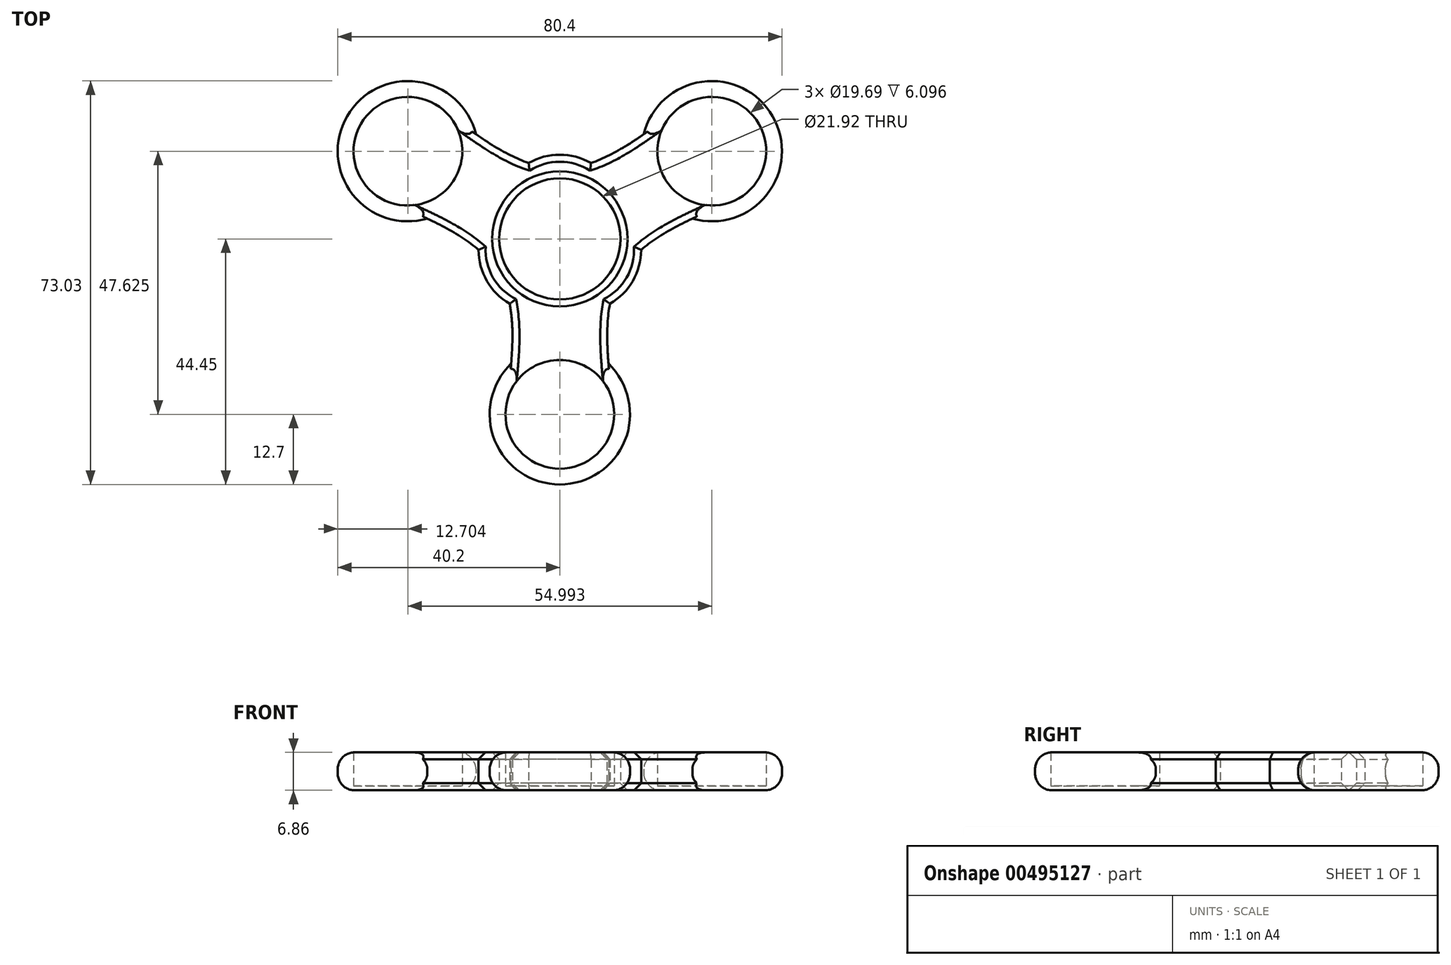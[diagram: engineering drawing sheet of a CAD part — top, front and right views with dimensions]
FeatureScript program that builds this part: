
annotation { "Feature Type Name" : "Feature", "Feature Type Description" : "" }
export const myFeature = defineFeature(function(context is Context, id is Id, definition is map)
    precondition{}
    {
        {
            var Q0;
            Q0=qCreatedBy(makeId("Top.planeOp"),FACE);
            var sketch = newSketch(context, id + "F0", { "sketchPlane" : qUnion([Q0])});
            skCircle(sketch, "E0", {"center": v(0, 0) * mm, "radius": 10.96 * mm});
            skCircle(sketch, "E1", {"center": v(0, 0) * mm, "radius": 12.7 * mm});
            skLineSegment(sketch, "E2", {"start": v(0, 0) * mm, "end": v(0, -12.7) * mm});
            skCircle(sketch, "E3.cCircle", {"center": v(0, 0) * mm, "radius": 12.7 * mm, "construction": true});
            skLineSegment(sketch, "E3.0", {"start": v(0, -12.7) * mm, "end": v(-11, 6.35) * mm});
            skLineSegment(sketch, "E3.1", {"start": v(-11, 6.35) * mm, "end": v(11, 6.35) * mm});
            skLineSegment(sketch, "E3.2", {"start": v(11, 6.35) * mm, "end": v(0, -12.7) * mm});
            skLineSegment(sketch, "E4", {"start": v(-11, 6.35) * mm, "end": v(0, 0) * mm});
            skLineSegment(sketch, "E5", {"start": v(0, 0) * mm, "end": v(11, 6.35) * mm});
            skLineSegment(sketch, "E6", {"start": v(-11, 6.35) * mm, "end": v(-27.5, 15.88) * mm});
            skLineSegment(sketch, "E7", {"start": v(11, 6.35) * mm, "end": v(27.5, 15.88) * mm});
            skLineSegment(sketch, "E8", {"start": v(0, -12.7) * mm, "end": v(0, -31.75) * mm});
            skCircle(sketch, "E9", {"center": v(-27.5, 15.87) * mm, "radius": 9.84 * mm});
            skCircle(sketch, "E10", {"center": v(27.5, 15.87) * mm, "radius": 9.84 * mm});
            skCircle(sketch, "E11", {"center": v(0, -31.75) * mm, "radius": 9.84 * mm});
            skLineSegment(sketch, "E12", {"start": v(-27.5, 15.87) * mm, "end": v(-32.42, 7.35) * mm});
            skLineSegment(sketch, "E13", {"start": v(-27.5, 15.87) * mm, "end": v(-22.58, 24.4) * mm});
            skLineSegment(sketch, "E14", {"start": v(27.5, 15.87) * mm, "end": v(22.58, 24.4) * mm});
            skLineSegment(sketch, "E15", {"start": v(27.5, 15.88) * mm, "end": v(32.42, 7.35) * mm});
            skLineSegment(sketch, "E16", {"start": v(0, -31.75) * mm, "end": v(-9.84, -31.75) * mm});
            skLineSegment(sketch, "E17", {"start": v(0, -31.75) * mm, "end": v(9.84, -31.75) * mm});
            skCircle(sketch, "E18", {"center": v(-27.5, 15.87) * mm, "radius": 12.7 * mm});
            skCircle(sketch, "E19", {"center": v(27.5, 15.87) * mm, "radius": 12.7 * mm});
            skCircle(sketch, "E20", {"center": v(0, -31.75) * mm, "radius": 12.7 * mm});
            skPoint(sketch, "E21", {"position": v(-5.5, -3.17) * mm});
            skPoint(sketch, "E22", {"position": v(0, 6.35) * mm});
            skPoint(sketch, "E23", {"position": v(5.5, -3.18) * mm});
            skLineSegment(sketch, "E24", {"start": v(-11, -6.35) * mm, "end": v(-13.18, -7.64) * mm});
            skLineSegment(sketch, "E25", {"start": v(11, -6.35) * mm, "end": v(13.2, -7.62) * mm});
            skArc(sketch, "E26", {"start": v(-11, 6.35) * mm, "mid": v(-13.2, -7.62) * mm, "end": v(0, -12.7) * mm});
            skArc(sketch, "E27", {"start": v(0, -12.7) * mm, "mid": v(13.2, -7.62) * mm, "end": v(11, 6.35) * mm});
            skLineSegment(sketch, "E28", {"start": v(0, 12.7) * mm, "end": v(0, 15.24) * mm});
            skArc(sketch, "E29", {"start": v(11, 6.35) * mm, "mid": v(0, 15.24) * mm, "end": v(-11, 6.35) * mm});
            skFitSpline(sketch, "E30", {"points": [v(-32.42, 7.35) * mm, v(-11, -6.35) * mm, v(-9.84, -31.75) * mm], "startDerivative": vector(52.41, -22.24) * mm, "endDerivative": vector(-6.95, -56.51) * mm});
            skFitSpline(sketch, "E31", {"points": [v(9.84, -31.75) * mm, v(11, -6.35) * mm, v(32.42, 7.35) * mm], "startDerivative": vector(-6.95, 56.51) * mm, "endDerivative": vector(52.41, 22.24) * mm});
            skFitSpline(sketch, "E32", {"points": [v(22.58, 24.4) * mm, v(0, 12.7) * mm, v(-22.58, 24.4) * mm], "startDerivative": vector(-45.47, -34.27) * mm, "endDerivative": vector(-45.47, 34.27) * mm});
            skSolve(sketch);
        }
        {
            var Q0;
            Q0 = qSketchRegion(id + "F0", true);
            var Q1;
            {var subQ1=sQuery(id+"F0.wireOp",EDGE,"E3.0");var subQ4=sQuery(id+"F0.wireOp",EDGE,"E0");var subQ8=makeQuery(id+"F0.imprint","INTERSECT",VERTEX,{"disambiguationData":[OD(0.0)],"derivedFrom":[subQ4,subQ1]});Q1=makeQuery(id+"F0.imprint","IMPRINT",FACE,{"disambiguationData":[TD([[makeQuery(id+"F0.imprint","IMPRINT",EDGE,{"disambiguationData":[TD([[subQ8,-1.0]])],"derivedFrom":subQ4}),-1.0]])]});}
            var Q2;
            {var subQ1=sQuery(id+"F0.wireOp",EDGE,"E3.1");var subQ4=sQuery(id+"F0.wireOp",EDGE,"E0");var subQ8=makeQuery(id+"F0.imprint","INTERSECT",VERTEX,{"disambiguationData":[OD(0.0)],"derivedFrom":[subQ4,subQ1]});Q2=makeQuery(id+"F0.imprint","IMPRINT",FACE,{"disambiguationData":[TD([[makeQuery(id+"F0.imprint","IMPRINT",EDGE,{"disambiguationData":[TD([[subQ8,-1.0]])],"derivedFrom":subQ4}),-1.0]])]});}
            var Q3;
            {var subQ1=sQuery(id+"F0.wireOp",EDGE,"E3.2");var subQ6=sQuery(id+"F0.wireOp",EDGE,"E0");var subQ8=makeQuery(id+"F0.imprint","INTERSECT",VERTEX,{"disambiguationData":[OD(0.0)],"derivedFrom":[subQ6,subQ1]});Q3=makeQuery(id+"F0.imprint","IMPRINT",FACE,{"disambiguationData":[TD([[makeQuery(id+"F0.imprint","IMPRINT",EDGE,{"disambiguationData":[TD([[subQ8,1.0]])],"derivedFrom":subQ6}),-1.0]])]});}
            var Q4;
            {var subQ0=sQuery(id+"F0.wireOp",EDGE,"E2");var subQ1=sQuery(id+"F0.wireOp",EDGE,"E0");var subQ2=makeQuery(id+"F0.imprint","INTERSECT",VERTEX,{"derivedFrom":[subQ1,subQ0]});Q4=makeQuery(id+"F0.imprint","IMPRINT",FACE,{"disambiguationData":[TD([[makeQuery(id+"F0.imprint","IMPRINT",EDGE,{"disambiguationData":[TD([[subQ2,-1.0]])],"derivedFrom":subQ1}),-1.0]])]});}
            var Q5;
            {var subQ0=sQuery(id+"F0.wireOp",EDGE,"E3.0");var subQ1=sQuery(id+"F0.wireOp",EDGE,"E0");var subQ2=makeQuery(id+"F0.imprint","INTERSECT",VERTEX,{"disambiguationData":[OD(1.0)],"derivedFrom":[subQ1,subQ0]});Q5=makeQuery(id+"F0.imprint","IMPRINT",FACE,{"disambiguationData":[TD([[makeQuery(id+"F0.imprint","IMPRINT",EDGE,{"disambiguationData":[TD([[subQ2,-1.0]])],"derivedFrom":subQ1}),-1.0]])]});}
            var Q6;
            {var subQ0=sQuery(id+"F0.wireOp",EDGE,"E5");var subQ1=sQuery(id+"F0.wireOp",EDGE,"E0");var subQ2=makeQuery(id+"F0.imprint","INTERSECT",VERTEX,{"derivedFrom":[subQ1,subQ0]});Q6=makeQuery(id+"F0.imprint","IMPRINT",FACE,{"disambiguationData":[TD([[makeQuery(id+"F0.imprint","IMPRINT",EDGE,{"disambiguationData":[TD([[subQ2,1.0]])],"derivedFrom":subQ1}),-1.0]])]});}
            var Q7;
            {var subQ0=sQuery(id+"F0.wireOp",EDGE,"E5");var subQ1=sQuery(id+"F0.wireOp",EDGE,"E0");var subQ2=makeQuery(id+"F0.imprint","INTERSECT",VERTEX,{"derivedFrom":[subQ1,subQ0]});Q7=makeQuery(id+"F0.imprint","IMPRINT",FACE,{"disambiguationData":[TD([[makeQuery(id+"F0.imprint","IMPRINT",EDGE,{"disambiguationData":[TD([[subQ2,-1.0]])],"derivedFrom":subQ1}),-1.0]])]});}
            var Q8;
            {var subQ0=sQuery(id+"F0.wireOp",EDGE,"E4");var subQ1=sQuery(id+"F0.wireOp",EDGE,"E0");var subQ2=makeQuery(id+"F0.imprint","INTERSECT",VERTEX,{"derivedFrom":[subQ1,subQ0]});Q8=makeQuery(id+"F0.imprint","IMPRINT",FACE,{"disambiguationData":[TD([[makeQuery(id+"F0.imprint","IMPRINT",EDGE,{"disambiguationData":[TD([[subQ2,-1.0]])],"derivedFrom":subQ1}),-1.0]])]});}
            var Q9;
            {var subQ0=sQuery(id+"F0.wireOp",EDGE,"E3.1");var subQ1=sQuery(id+"F0.wireOp",EDGE,"E0");var subQ2=makeQuery(id+"F0.imprint","INTERSECT",VERTEX,{"disambiguationData":[OD(1.0)],"derivedFrom":[subQ1,subQ0]});Q9=makeQuery(id+"F0.imprint","IMPRINT",FACE,{"disambiguationData":[TD([[makeQuery(id+"F0.imprint","IMPRINT",EDGE,{"disambiguationData":[TD([[subQ2,-1.0]])],"derivedFrom":subQ1}),-1.0]])]});}
            extrude(context, id + "F1", {"entities" : qUnion([Q0, Q1, Q2, Q3, Q4, Q5, Q6, Q7, Q8, Q9]), "depth" : 6.86 * mm, "offsetDistance" : 25.4 * mm});
        }
        {
            var Q0;
            Q0=makeQuery(id+"F1.opExtrude","CAP_EDGE",EDGE,{"disambiguationData":[OSD([sQuery(id+"F0.wireOp",EDGE,"E0")])],"isStart":true});
            var Q1;
            Q1=makeQuery(id+"F1.opExtrude","CAP_EDGE",EDGE,{"disambiguationData":[OSD([sQuery(id+"F0.wireOp",EDGE,"E0")])],"isStart":false});
            chamfer(context, id + "F2", {"entities" : qUnion([Q0, Q1]), "width" : 1.27 * mm, "tangentPropagation" : true});
        }
        {
            var Q0;
            {var subQ0=sQuery(id+"F0.wireOp",EDGE,"E31");Q0=makeQuery(id+"F1.opExtrude","CAP_EDGE",EDGE,{"disambiguationData":[OSD([subQ0]),TDD([makeQuery(id+"F0.imprint","IMPRINT",EDGE,{"disambiguationData":[TD([[makeQuery(id+"F0.imprint","INTERSECT",VERTEX,{"derivedFrom":[sQuery(id+"F0.wireOp",EDGE,"E20"),subQ0]}),-1.0]])],"derivedFrom":subQ0})])],"isStart":false});}
            var Q1;
            Q1=makeQuery(id+"F1.opExtrude","CAP_EDGE",EDGE,{"disambiguationData":[OSD([sQuery(id+"F0.wireOp",EDGE,"E27")])],"isStart":false});
            var Q2;
            {var subQ0=sQuery(id+"F0.wireOp",EDGE,"E31");Q2=makeQuery(id+"F1.opExtrude","CAP_EDGE",EDGE,{"disambiguationData":[OSD([subQ0]),TDD([makeQuery(id+"F0.imprint","IMPRINT",EDGE,{"disambiguationData":[TD([[makeQuery(id+"F0.imprint","INTERSECT",VERTEX,{"derivedFrom":[sQuery(id+"F0.wireOp",EDGE,"E19"),subQ0]}),1.0]])],"derivedFrom":subQ0})])],"isStart":false});}
            var Q3;
            {var subQ0=sQuery(id+"F0.wireOp",EDGE,"E32");Q3=makeQuery(id+"F1.opExtrude","CAP_EDGE",EDGE,{"disambiguationData":[OSD([subQ0]),TDD([makeQuery(id+"F0.imprint","IMPRINT",EDGE,{"disambiguationData":[TD([[makeQuery(id+"F0.imprint","INTERSECT",VERTEX,{"derivedFrom":[sQuery(id+"F0.wireOp",EDGE,"E19"),subQ0]}),-1.0]])],"derivedFrom":subQ0})])],"isStart":false});}
            var Q4;
            Q4=makeQuery(id+"F1.opExtrude","CAP_EDGE",EDGE,{"disambiguationData":[OSD([sQuery(id+"F0.wireOp",EDGE,"E29")])],"isStart":false});
            var Q5;
            {var subQ0=sQuery(id+"F0.wireOp",EDGE,"E32");Q5=makeQuery(id+"F1.opExtrude","CAP_EDGE",EDGE,{"disambiguationData":[OSD([subQ0]),TDD([makeQuery(id+"F0.imprint","IMPRINT",EDGE,{"disambiguationData":[TD([[makeQuery(id+"F0.imprint","INTERSECT",VERTEX,{"derivedFrom":[sQuery(id+"F0.wireOp",EDGE,"E18"),subQ0]}),1.0]])],"derivedFrom":subQ0})])],"isStart":false});}
            var Q6;
            {var subQ0=sQuery(id+"F0.wireOp",EDGE,"E30");Q6=makeQuery(id+"F1.opExtrude","CAP_EDGE",EDGE,{"disambiguationData":[OSD([subQ0]),TDD([makeQuery(id+"F0.imprint","IMPRINT",EDGE,{"disambiguationData":[TD([[makeQuery(id+"F0.imprint","INTERSECT",VERTEX,{"derivedFrom":[sQuery(id+"F0.wireOp",EDGE,"E18"),subQ0]}),-1.0]])],"derivedFrom":subQ0})])],"isStart":false});}
            var Q7;
            {var subQ0=sQuery(id+"F0.wireOp",EDGE,"E30");Q7=makeQuery(id+"F1.opExtrude","CAP_EDGE",EDGE,{"disambiguationData":[OSD([subQ0]),TDD([makeQuery(id+"F0.imprint","IMPRINT",EDGE,{"disambiguationData":[TD([[makeQuery(id+"F0.imprint","INTERSECT",VERTEX,{"derivedFrom":[sQuery(id+"F0.wireOp",EDGE,"E18"),subQ0]}),-1.0]])],"derivedFrom":subQ0})])],"isStart":true});}
            var Q8;
            Q8=makeQuery(id+"F1.opExtrude","CAP_EDGE",EDGE,{"disambiguationData":[OSD([sQuery(id+"F0.wireOp",EDGE,"E26")])],"isStart":true});
            var Q9;
            Q9=makeQuery(id+"F1.opExtrude","CAP_EDGE",EDGE,{"disambiguationData":[OSD([sQuery(id+"F0.wireOp",EDGE,"E26")])],"isStart":false});
            var Q10;
            {var subQ0=sQuery(id+"F0.wireOp",EDGE,"E30");Q10=makeQuery(id+"F1.opExtrude","CAP_EDGE",EDGE,{"disambiguationData":[OSD([subQ0]),TDD([makeQuery(id+"F0.imprint","IMPRINT",EDGE,{"disambiguationData":[TD([[makeQuery(id+"F0.imprint","INTERSECT",VERTEX,{"derivedFrom":[sQuery(id+"F0.wireOp",EDGE,"E20"),subQ0]}),1.0]])],"derivedFrom":subQ0})])],"isStart":true});}
            var Q11;
            {var subQ0=sQuery(id+"F0.wireOp",EDGE,"E30");Q11=makeQuery(id+"F1.opExtrude","CAP_EDGE",EDGE,{"disambiguationData":[OSD([subQ0]),TDD([makeQuery(id+"F0.imprint","IMPRINT",EDGE,{"disambiguationData":[TD([[makeQuery(id+"F0.imprint","INTERSECT",VERTEX,{"derivedFrom":[sQuery(id+"F0.wireOp",EDGE,"E20"),subQ0]}),1.0]])],"derivedFrom":subQ0})])],"isStart":false});}
            var Q12;
            {var subQ0=sQuery(id+"F0.wireOp",EDGE,"E31");Q12=makeQuery(id+"F1.opExtrude","CAP_EDGE",EDGE,{"disambiguationData":[OSD([subQ0]),TDD([makeQuery(id+"F0.imprint","IMPRINT",EDGE,{"disambiguationData":[TD([[makeQuery(id+"F0.imprint","INTERSECT",VERTEX,{"derivedFrom":[sQuery(id+"F0.wireOp",EDGE,"E20"),subQ0]}),-1.0]])],"derivedFrom":subQ0})])],"isStart":true});}
            var Q13;
            Q13=makeQuery(id+"F1.opExtrude","CAP_EDGE",EDGE,{"disambiguationData":[OSD([sQuery(id+"F0.wireOp",EDGE,"E27")])],"isStart":true});
            var Q14;
            {var subQ0=sQuery(id+"F0.wireOp",EDGE,"E31");Q14=makeQuery(id+"F1.opExtrude","CAP_EDGE",EDGE,{"disambiguationData":[OSD([subQ0]),TDD([makeQuery(id+"F0.imprint","IMPRINT",EDGE,{"disambiguationData":[TD([[makeQuery(id+"F0.imprint","INTERSECT",VERTEX,{"derivedFrom":[sQuery(id+"F0.wireOp",EDGE,"E19"),subQ0]}),1.0]])],"derivedFrom":subQ0})])],"isStart":true});}
            var Q15;
            {var subQ0=sQuery(id+"F0.wireOp",EDGE,"E32");Q15=makeQuery(id+"F1.opExtrude","CAP_EDGE",EDGE,{"disambiguationData":[OSD([subQ0]),TDD([makeQuery(id+"F0.imprint","IMPRINT",EDGE,{"disambiguationData":[TD([[makeQuery(id+"F0.imprint","INTERSECT",VERTEX,{"derivedFrom":[sQuery(id+"F0.wireOp",EDGE,"E19"),subQ0]}),-1.0]])],"derivedFrom":subQ0})])],"isStart":true});}
            var Q16;
            Q16=makeQuery(id+"F1.opExtrude","CAP_EDGE",EDGE,{"disambiguationData":[OSD([sQuery(id+"F0.wireOp",EDGE,"E29")])],"isStart":true});
            var Q17;
            {var subQ0=sQuery(id+"F0.wireOp",EDGE,"E32");Q17=makeQuery(id+"F1.opExtrude","CAP_EDGE",EDGE,{"disambiguationData":[OSD([subQ0]),TDD([makeQuery(id+"F0.imprint","IMPRINT",EDGE,{"disambiguationData":[TD([[makeQuery(id+"F0.imprint","INTERSECT",VERTEX,{"derivedFrom":[sQuery(id+"F0.wireOp",EDGE,"E18"),subQ0]}),1.0]])],"derivedFrom":subQ0})])],"isStart":true});}
            chamfer(context, id + "F3", {"entities" : qUnion([Q0, Q1, Q2, Q3, Q4, Q5, Q6, Q7, Q8, Q9, Q10, Q11, Q12, Q13, Q14, Q15, Q16, Q17]), "width" : 1.27 * mm, "tangentPropagation" : true});
        }
        {
            var Q0;
            {var subQ0=sQuery(id+"F0.wireOp",EDGE,"E12");Q0=makeQuery(id+"F0.imprint","IMPRINT",FACE,{"disambiguationData":[TD([[makeQuery(id+"F0.imprint","IMPRINT",EDGE,{"derivedFrom":subQ0}),-1.0]])]});}
            var Q1;
            {var subQ0=sQuery(id+"F0.wireOp",EDGE,"E12");Q1=makeQuery(id+"F0.imprint","IMPRINT",FACE,{"disambiguationData":[TD([[makeQuery(id+"F0.imprint","IMPRINT",EDGE,{"derivedFrom":subQ0}),1.0]])]});}
            var Q2;
            {var subQ0=sQuery(id+"F0.wireOp",EDGE,"E13");Q2=makeQuery(id+"F0.imprint","IMPRINT",FACE,{"disambiguationData":[TD([[makeQuery(id+"F0.imprint","IMPRINT",EDGE,{"derivedFrom":subQ0}),-1.0]])]});}
            var Q3;
            {var subQ0=sQuery(id+"F0.wireOp",EDGE,"E14");Q3=makeQuery(id+"F0.imprint","IMPRINT",FACE,{"disambiguationData":[TD([[makeQuery(id+"F0.imprint","IMPRINT",EDGE,{"derivedFrom":subQ0}),1.0]])]});}
            var Q4;
            {var subQ0=sQuery(id+"F0.wireOp",EDGE,"E14");Q4=makeQuery(id+"F0.imprint","IMPRINT",FACE,{"disambiguationData":[TD([[makeQuery(id+"F0.imprint","IMPRINT",EDGE,{"derivedFrom":subQ0}),-1.0]])]});}
            var Q5;
            {var subQ0=sQuery(id+"F0.wireOp",EDGE,"E15");Q5=makeQuery(id+"F0.imprint","IMPRINT",FACE,{"disambiguationData":[TD([[makeQuery(id+"F0.imprint","IMPRINT",EDGE,{"derivedFrom":subQ0}),-1.0]])]});}
            var Q6;
            {var subQ0=sQuery(id+"F0.wireOp",EDGE,"E16");Q6=makeQuery(id+"F0.imprint","IMPRINT",FACE,{"disambiguationData":[TD([[makeQuery(id+"F0.imprint","IMPRINT",EDGE,{"derivedFrom":subQ0}),-1.0]])]});}
            var Q7;
            {var subQ0=sQuery(id+"F0.wireOp",EDGE,"E17");Q7=makeQuery(id+"F0.imprint","IMPRINT",FACE,{"disambiguationData":[TD([[makeQuery(id+"F0.imprint","IMPRINT",EDGE,{"derivedFrom":subQ0}),1.0]])]});}
            var Q8;
            {var subQ0=sQuery(id+"F0.wireOp",EDGE,"E16");Q8=makeQuery(id+"F0.imprint","IMPRINT",FACE,{"disambiguationData":[TD([[makeQuery(id+"F0.imprint","IMPRINT",EDGE,{"derivedFrom":subQ0}),1.0]])]});}
            var Q9;
            {var subQ0=sQuery(id+"F0.wireOp",EDGE,"E32");var subQ1=sQuery(id+"F0.wireOp",EDGE,"E10");var subQ3=makeQuery(id+"F0.imprint","INTERSECT",VERTEX,{"derivedFrom":[subQ1,subQ0]});Q9=makeQuery(id+"F0.imprint","IMPRINT",FACE,{"disambiguationData":[TD([[makeQuery(id+"F0.imprint","IMPRINT",EDGE,{"disambiguationData":[TD([[subQ3,1.0]])],"derivedFrom":subQ1}),1.0]])]});}
            var Q10;
            {var subQ0=sQuery(id+"F0.wireOp",EDGE,"E31");var subQ1=sQuery(id+"F0.wireOp",EDGE,"E10");var subQ3=makeQuery(id+"F0.imprint","INTERSECT",VERTEX,{"derivedFrom":[subQ1,subQ0]});Q10=makeQuery(id+"F0.imprint","IMPRINT",FACE,{"disambiguationData":[TD([[makeQuery(id+"F0.imprint","IMPRINT",EDGE,{"disambiguationData":[TD([[subQ3,-1.0]])],"derivedFrom":subQ1}),1.0]])]});}
            var Q11;
            {var subQ0=sQuery(id+"F0.wireOp",EDGE,"E32");var subQ1=sQuery(id+"F0.wireOp",EDGE,"E9");var subQ3=makeQuery(id+"F0.imprint","INTERSECT",VERTEX,{"derivedFrom":[subQ1,subQ0]});Q11=makeQuery(id+"F0.imprint","IMPRINT",FACE,{"disambiguationData":[TD([[makeQuery(id+"F0.imprint","IMPRINT",EDGE,{"disambiguationData":[TD([[subQ3,-1.0]])],"derivedFrom":subQ1}),1.0]])]});}
            var Q12;
            {var subQ0=sQuery(id+"F0.wireOp",EDGE,"E30");var subQ1=sQuery(id+"F0.wireOp",EDGE,"E9");var subQ3=makeQuery(id+"F0.imprint","INTERSECT",VERTEX,{"derivedFrom":[subQ1,subQ0]});Q12=makeQuery(id+"F0.imprint","IMPRINT",FACE,{"disambiguationData":[TD([[makeQuery(id+"F0.imprint","IMPRINT",EDGE,{"disambiguationData":[TD([[subQ3,1.0]])],"derivedFrom":subQ1}),1.0]])]});}
            var Q13;
            {var subQ0=sQuery(id+"F0.wireOp",EDGE,"E30");var subQ1=sQuery(id+"F0.wireOp",EDGE,"E11");var subQ3=makeQuery(id+"F0.imprint","INTERSECT",VERTEX,{"derivedFrom":[subQ1,subQ0]});Q13=makeQuery(id+"F0.imprint","IMPRINT",FACE,{"disambiguationData":[TD([[makeQuery(id+"F0.imprint","IMPRINT",EDGE,{"disambiguationData":[TD([[subQ3,-1.0]])],"derivedFrom":subQ1}),1.0]])]});}
            var Q14;
            {var subQ0=sQuery(id+"F0.wireOp",EDGE,"E31");var subQ1=sQuery(id+"F0.wireOp",EDGE,"E11");var subQ3=makeQuery(id+"F0.imprint","INTERSECT",VERTEX,{"derivedFrom":[subQ1,subQ0]});Q14=makeQuery(id+"F0.imprint","IMPRINT",FACE,{"disambiguationData":[TD([[makeQuery(id+"F0.imprint","IMPRINT",EDGE,{"disambiguationData":[TD([[subQ3,1.0]])],"derivedFrom":subQ1}),1.0]])]});}
            extrude(context, id + "F4", {"entities" : qUnion([Q0, Q1, Q2, Q3, Q4, Q5, Q6, Q7, Q8, Q9, Q10, Q11, Q12, Q13, Q14]), "operationType" : NewBodyOperationType.ADD, "depth" : 0.76 * mm});
        }
        {
            var Q0;
            Q0=makeQuery(id+"F1.opExtrude","CAP_EDGE",EDGE,{"disambiguationData":[OSD([sQuery(id+"F0.wireOp",EDGE,"E19")])],"isStart":false});
            var Q1;
            Q1=makeQuery(id+"F1.opExtrude","CAP_EDGE",EDGE,{"disambiguationData":[OSD([sQuery(id+"F0.wireOp",EDGE,"E19")])],"isStart":true});
            var Q2;
            Q2=makeQuery(id+"F1.opExtrude","CAP_EDGE",EDGE,{"disambiguationData":[OSD([sQuery(id+"F0.wireOp",EDGE,"E18")])],"isStart":false});
            var Q3;
            Q3=makeQuery(id+"F1.opExtrude","CAP_EDGE",EDGE,{"disambiguationData":[OSD([sQuery(id+"F0.wireOp",EDGE,"E18")])],"isStart":true});
            var Q4;
            Q4=makeQuery(id+"F1.opExtrude","CAP_EDGE",EDGE,{"disambiguationData":[OSD([sQuery(id+"F0.wireOp",EDGE,"E20")])],"isStart":false});
            var Q5;
            Q5=makeQuery(id+"F1.opExtrude","CAP_EDGE",EDGE,{"disambiguationData":[OSD([sQuery(id+"F0.wireOp",EDGE,"E20")])],"isStart":true});
            fillet(context, id + "F5", {"entities" : qUnion([Q0, Q1, Q2, Q3, Q4, Q5]), "radius" : 3.05 * mm, "tangentPropagation" : true, "allowEdgeOverflow" : false});
        }
    });
